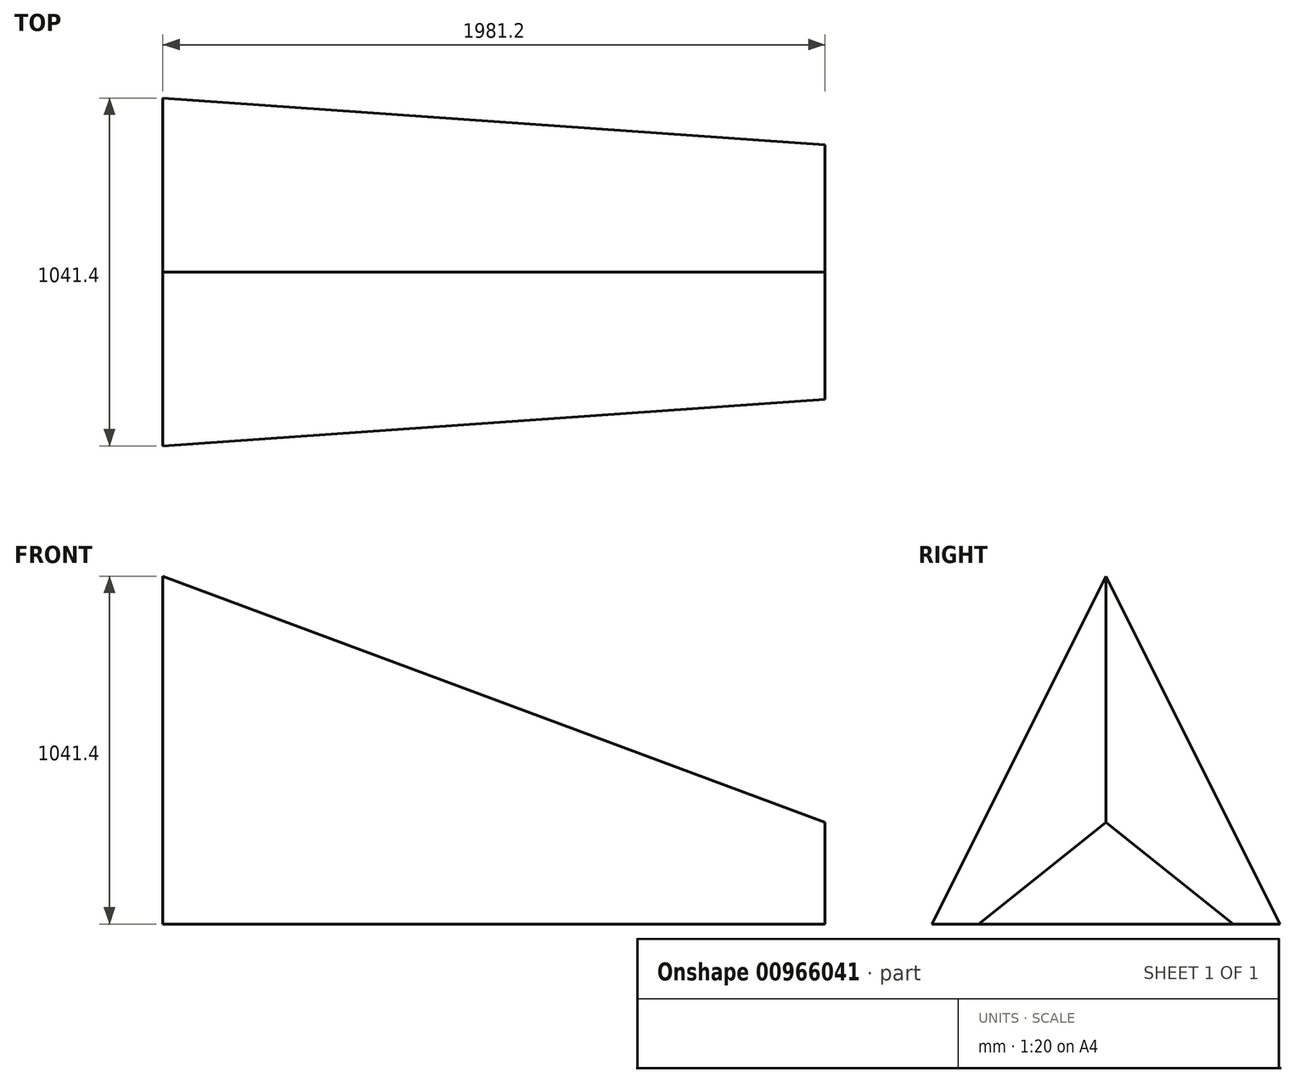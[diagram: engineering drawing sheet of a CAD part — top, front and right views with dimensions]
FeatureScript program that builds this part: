
annotation { "Feature Type Name" : "Feature", "Feature Type Description" : "" }
export const myFeature = defineFeature(function(context is Context, id is Id, definition is map)
    precondition{}
    {
        {
            var Q0;
            Q0=qCreatedBy(makeId("Top.planeOp"),FACE);
            var sketch = newSketch(context, id + "F0", { "sketchPlane" : qUnion([Q0])});
            skLineSegment(sketch, "E0.bottom", {"start": v(914.4, 254) * mm, "end": v(-914.4, 254) * mm});
            skLineSegment(sketch, "E0.top", {"start": v(914.4, -254) * mm, "end": v(-914.4, -254) * mm});
            skLineSegment(sketch, "E0.left", {"start": v(914.4, 254) * mm, "end": v(914.4, -254) * mm});
            skLineSegment(sketch, "E0.right", {"start": v(-914.4, 254) * mm, "end": v(-914.4, -254) * mm});
            skPoint(sketch, "E0.middle", {"position": v(0, 0) * mm});
            skSolve(sketch);
        }
        {
            var Q0;
            Q0=qCreatedBy(makeId("Top.planeOp"),FACE);
            var sketch = newSketch(context, id + "F1", { "sketchPlane" : qUnion([Q0])});
            skLineSegment(sketch, "E1", {"start": v(-914.4, 520.7) * mm, "end": v(-914.4, -520.7) * mm, "construction": true});
            skPoint(sketch, "E2", {"position": v(-914.4, 0) * mm});
            skLineSegment(sketch, "E3", {"start": v(-1879.6, 0) * mm, "end": v(1066.8, 0) * mm, "construction": true});
            skLineSegment(sketch, "E4", {"start": v(1066.8, 381) * mm, "end": v(1066.8, -381) * mm, "construction": true});
            skLineSegment(sketch, "E5", {"start": v(-1879.6, 0) * mm, "end": v(-914.4, 520.7) * mm, "construction": true});
            skLineSegment(sketch, "E6", {"start": v(-914.4, 520.7) * mm, "end": v(1066.8, 381) * mm, "construction": true});
            skLineSegment(sketch, "E7", {"start": v(1066.8, -381) * mm, "end": v(-914.4, -520.7) * mm, "construction": true});
            skLineSegment(sketch, "E8", {"start": v(-1879.6, 0) * mm, "end": v(-914.4, -520.7) * mm, "construction": true});
            skSolve(sketch);
        }
        {
            var Q0;
            Q0=qCreatedBy(makeId("Front.planeOp"),FACE);
            var sketch = newSketch(context, id + "F2", { "sketchPlane" : qUnion([Q0])});
            skPoint(sketch, "E9.0", {"position": v(-914.4, 0) * mm});
            skPoint(sketch, "E10.0", {"position": v(-1879.6, 0) * mm});
            skPoint(sketch, "E11.0", {"position": v(1066.8, 0) * mm});
            skLineSegment(sketch, "E12", {"start": v(-914.4, 0) * mm, "end": v(-914.4, 1041.4) * mm, "construction": true});
            skLineSegment(sketch, "E13", {"start": v(-914.4, 1041.4) * mm, "end": v(-1879.6, 0) * mm, "construction": true});
            skLineSegment(sketch, "E14", {"start": v(1066.8, 0) * mm, "end": v(1066.8, 304.8) * mm, "construction": true});
            skLineSegment(sketch, "E15", {"start": v(1066.8, 304.8) * mm, "end": v(-914.4, 1041.4) * mm, "construction": true});
            skSolve(sketch);
        }
        {
            var Q0;
            Q0=sQuery(id+"F1.wireOp",EDGE,"E1");
            var Q1;
            Q1=sQuery(id+"F2.wireOp",EDGE,"E12");
            cPlane(context, id + "F3", {"entities" : qUnion([Q0, Q1]), "cplaneType" : CPlaneType.LINE_ANGLE, "offset" : 25.4 * mm, "angle" : 0 * degree, "width" : 152.4 * mm, "height" : 152.4 * mm});
        }
        {
            var Q0;
            Q0=sQuery(id+"F1.wireOp",EDGE,"E4");
            var Q1;
            Q1=sQuery(id+"F2.wireOp",EDGE,"E14");
            cPlane(context, id + "F4", {"entities" : qUnion([Q0, Q1]), "cplaneType" : CPlaneType.LINE_ANGLE, "offset" : 25.4 * mm, "angle" : 0 * degree, "width" : 152.4 * mm, "height" : 152.4 * mm});
        }
        {
            var Q0;
            Q0=qCreatedBy(id+"F3.planeOp",FACE);
            var sketch = newSketch(context, id + "F5", { "sketchPlane" : qUnion([Q0])});
            skPoint(sketch, "E16.0", {"position": v(-520.7, 0) * mm});
            skPoint(sketch, "E17.0", {"position": v(520.7, 0) * mm});
            skPoint(sketch, "E18.0", {"position": v(0, 1041.4) * mm});
            skLineSegment(sketch, "E19", {"start": v(-520.7, 0) * mm, "end": v(520.7, 0) * mm});
            skLineSegment(sketch, "E20", {"start": v(0, 1041.4) * mm, "end": v(520.7, 0) * mm});
            skLineSegment(sketch, "E21", {"start": v(-520.7, 0) * mm, "end": v(0, 1041.4) * mm});
            skSolve(sketch);
        }
        {
            var Q0;
            Q0=qCreatedBy(id+"F4.planeOp",FACE);
            var sketch = newSketch(context, id + "F6", { "sketchPlane" : qUnion([Q0])});
            skPoint(sketch, "E22.0", {"position": v(-381, 0) * mm});
            skPoint(sketch, "E23.0", {"position": v(381, 0) * mm});
            skPoint(sketch, "E24.0", {"position": v(0, 304.8) * mm});
            skLineSegment(sketch, "E25", {"start": v(-381, 0) * mm, "end": v(381, 0) * mm});
            skLineSegment(sketch, "E26", {"start": v(381, 0) * mm, "end": v(0, 304.8) * mm});
            skLineSegment(sketch, "E27", {"start": v(0, 304.8) * mm, "end": v(-381, 0) * mm});
            skSolve(sketch);
        }
        {
            var Q0;
            Q0=makeQuery(id+"F6.imprint","IMPRINT",FACE,{"disambiguationData":[TD([[makeQuery(id+"F6.imprint","IMPRINT",EDGE,{"derivedFrom":sQuery(id+"F6.wireOp",EDGE,"E25")}),1.0]])]});
            var Q1;
            Q1=makeQuery(id+"F5.imprint","IMPRINT",FACE,{"disambiguationData":[TD([[makeQuery(id+"F5.imprint","IMPRINT",EDGE,{"derivedFrom":sQuery(id+"F5.wireOp",EDGE,"E19")}),1.0]])]});
            loft(context, id + "F7", {"sheetProfilesArray" : [{ "sheetProfileEntities" : qUnion([Q0]) }, { "sheetProfileEntities" : qUnion([Q1]) }]});
        }
    });
